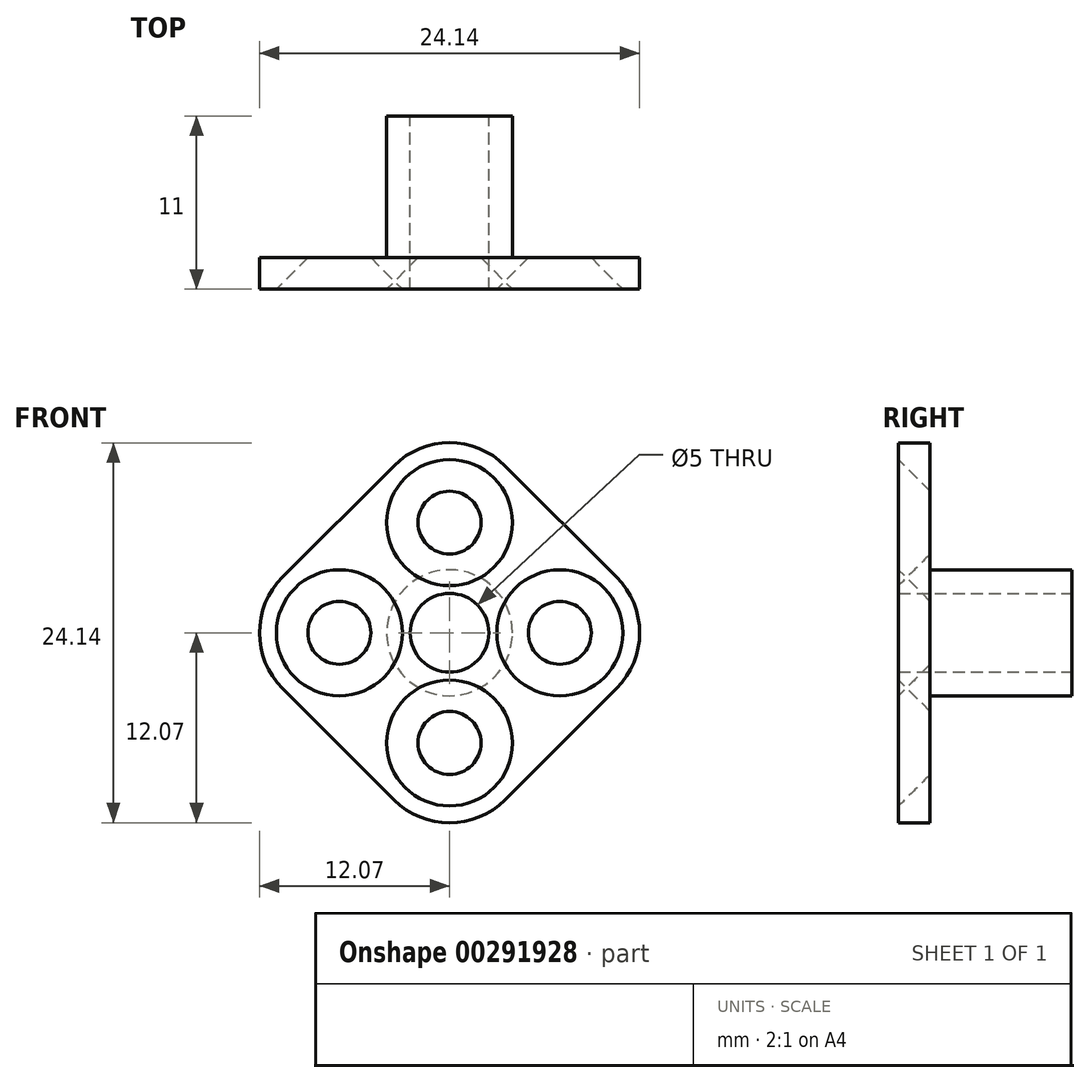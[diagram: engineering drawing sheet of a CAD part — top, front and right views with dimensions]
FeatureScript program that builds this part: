
annotation { "Feature Type Name" : "Feature", "Feature Type Description" : "" }
export const myFeature = defineFeature(function(context is Context, id is Id, definition is map)
    precondition{}
    {
        {
            var Q0;
            Q0=qCreatedBy(makeId("Front.planeOp"),FACE);
            var sketch = newSketch(context, id + "F0", { "sketchPlane" : qUnion([Q0])});
            skPoint(sketch, "E0.middle", {"position": v(0, 0) * mm});
            skCircle(sketch, "E1", {"center": v(0, 0) * mm, "radius": 2.5 * mm});
            skCircle(sketch, "E2", {"center": v(7, 0) * mm, "radius": 2 * mm});
            skCircle(sketch, "E3.1.0", {"center": v(0, 7) * mm, "radius": 2 * mm});
            skCircle(sketch, "E3.2.0", {"center": v(-7, 0) * mm, "radius": 2 * mm});
            skCircle(sketch, "E3.3.0", {"center": v(0, -7) * mm, "radius": 2 * mm});
            skPoint(sketch, "E4.endSnap0", {"position": v(0, -11.8) * mm});
            skLineSegment(sketch, "E5.bottom", {"start": v(-3.54, -10.6) * mm, "end": v(-10.6, -3.54) * mm});
            skLineSegment(sketch, "E5.top", {"start": v(10.6, 3.54) * mm, "end": v(3.54, 10.6) * mm});
            skLineSegment(sketch, "E5.left", {"start": v(3.54, -10.6) * mm, "end": v(10.6, -3.54) * mm});
            skLineSegment(sketch, "E5.right", {"start": v(-10.6, 3.54) * mm, "end": v(-3.54, 10.6) * mm});
            skPoint(sketch, "E6.visualSharp", {"position": v(0, -14.14) * mm});
            skArc(sketch, "E6.filletArc", {"start": v(-3.54, -10.6) * mm, "mid": v(0, -12.07) * mm, "end": v(3.54, -10.6) * mm});
            skPoint(sketch, "E7.visualSharp", {"position": v(-14.14, 0) * mm});
            skArc(sketch, "E7.filletArc", {"start": v(-10.6, 3.54) * mm, "mid": v(-12.07, 0) * mm, "end": v(-10.6, -3.54) * mm});
            skPoint(sketch, "E8.visualSharp", {"position": v(0, 14.14) * mm});
            skArc(sketch, "E8.filletArc", {"start": v(3.54, 10.6) * mm, "mid": v(0, 12.07) * mm, "end": v(-3.54, 10.6) * mm});
            skPoint(sketch, "E9.visualSharp", {"position": v(14.14, 0) * mm});
            skArc(sketch, "E9.filletArc", {"start": v(10.6, -3.54) * mm, "mid": v(12.07, 0) * mm, "end": v(10.6, 3.54) * mm});
            skSolve(sketch);
        }
        {
            var Q0;
            Q0=qSketchRegion(id+"F0",true);
            extrude(context, id + "F1", {"entities" : qUnion([Q0]), "depth" : 2 * mm});
        }
        {
            var Q0;
            Q0=makeQuery(id+"F1.opExtrude","CAP_EDGE",EDGE,{"disambiguationData":[OSD([sQuery(id+"F0.wireOp",EDGE,"E2")])],"isStart":false});
            var Q1;
            Q1=makeQuery(id+"F1.opExtrude","CAP_EDGE",EDGE,{"disambiguationData":[OSD([sQuery(id+"F0.wireOp",EDGE,"E3.3.0")])],"isStart":false});
            var Q2;
            Q2=makeQuery(id+"F1.opExtrude","CAP_EDGE",EDGE,{"disambiguationData":[OSD([sQuery(id+"F0.wireOp",EDGE,"E3.2.0")])],"isStart":false});
            var Q3;
            Q3=makeQuery(id+"F1.opExtrude","CAP_EDGE",EDGE,{"disambiguationData":[OSD([sQuery(id+"F0.wireOp",EDGE,"E3.1.0")])],"isStart":false});
            chamfer(context, id + "F2", {"entities" : qUnion([Q0, Q1, Q2, Q3]), "width" : 2 * mm, "tangentPropagation" : true});
        }
        {
            var Q0;
            Q0=makeQuery(id+"F1.opExtrude","CAP_FACE",FACE,{"disambiguationData":[OSD([sQuery(id+"F0.wireOp",EDGE,"E1"),sQuery(id+"F0.wireOp",EDGE,"E2"),sQuery(id+"F0.wireOp",EDGE,"E3.1.0"),sQuery(id+"F0.wireOp",EDGE,"E3.2.0"),sQuery(id+"F0.wireOp",EDGE,"E3.3.0"),sQuery(id+"F0.wireOp",EDGE,"E5.bottom"),sQuery(id+"F0.wireOp",EDGE,"E5.top"),sQuery(id+"F0.wireOp",EDGE,"E5.left"),sQuery(id+"F0.wireOp",EDGE,"E5.right"),sQuery(id+"F0.wireOp",EDGE,"E6.filletArc"),sQuery(id+"F0.wireOp",EDGE,"E7.filletArc"),sQuery(id+"F0.wireOp",EDGE,"E8.filletArc"),sQuery(id+"F0.wireOp",EDGE,"E9.filletArc")])],"isStart":true});
            var sketch = newSketch(context, id + "F3", { "sketchPlane" : qUnion([Q0])});
            skCircle(sketch, "E10", {"center": v(0, 0) * mm, "radius": 4 * mm});
            skSolve(sketch);
        }
        {
            var Q0;
            Q0=makeQuery(id+"F3.imprint","IMPRINT",FACE,{"disambiguationData":[TD([[makeQuery(id+"F3.imprint","IMPRINT",EDGE,{"derivedFrom":sQuery(id+"F3.wireOp",EDGE,"E10")}),1.0]])]});
            extrude(context, id + "F4", {"entities" : qUnion([Q0]), "operationType" : NewBodyOperationType.ADD, "depth" : 9 * mm, "offsetDistance" : 25 * mm});
        }
    });
